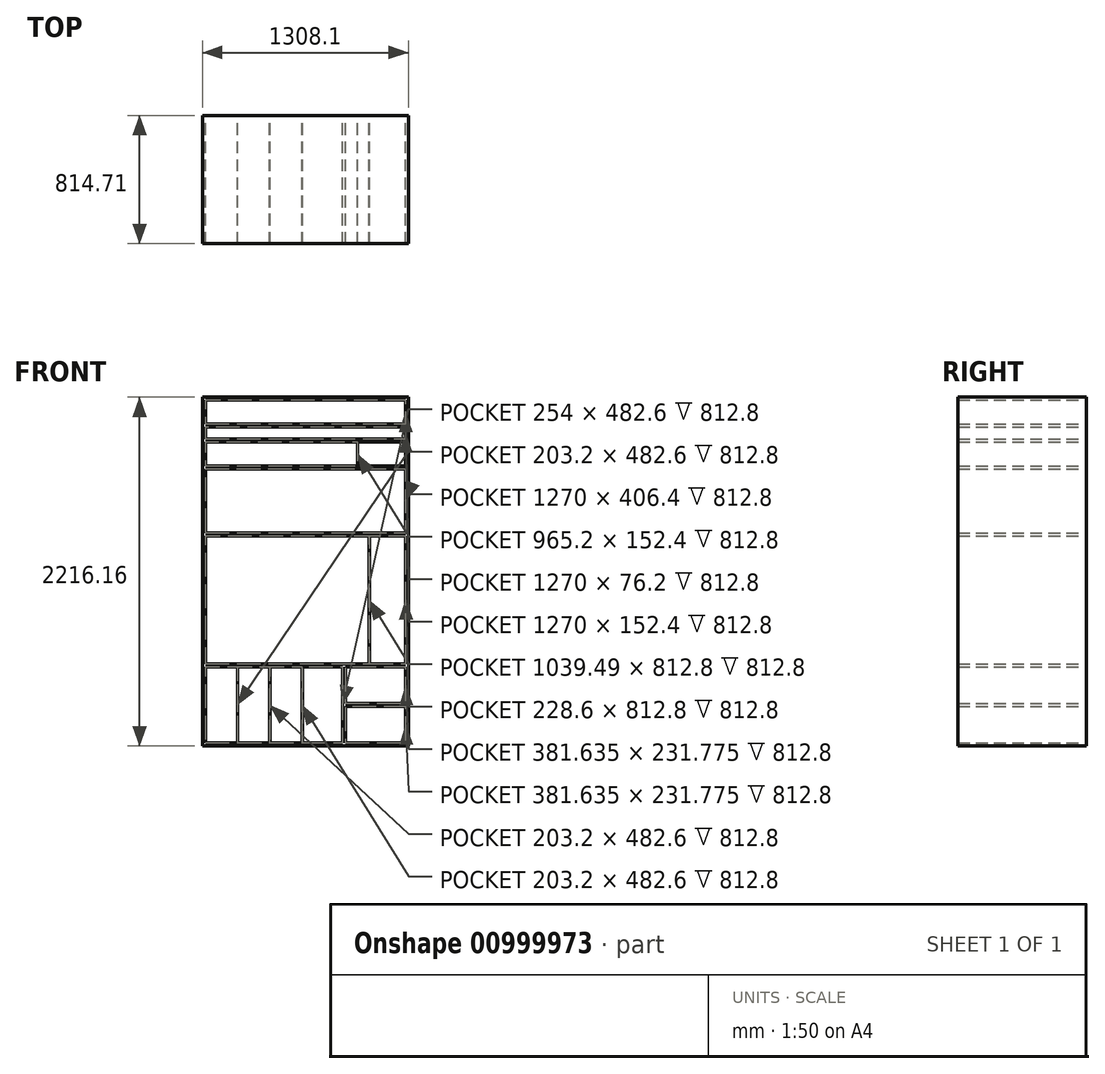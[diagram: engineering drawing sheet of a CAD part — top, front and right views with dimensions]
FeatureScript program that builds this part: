
annotation { "Feature Type Name" : "Feature", "Feature Type Description" : "" }
export const myFeature = defineFeature(function(context is Context, id is Id, definition is map)
    precondition{}
    {
        {
            var Q0;
            Q0=qCreatedBy(makeId("Front.planeOp"),FACE);
            var sketch = newSketch(context, id + "F0", { "sketchPlane" : qUnion([Q0])});
            skLineSegment(sketch, "E0.bottom", {"start": v(-635, 415.93) * mm, "end": v(635, 415.93) * mm});
            skLineSegment(sketch, "E0.top", {"start": v(-635, -415.93) * mm, "end": v(635, -415.92) * mm});
            skLineSegment(sketch, "E0.left", {"start": v(-635, 415.93) * mm, "end": v(-635, -415.93) * mm});
            skLineSegment(sketch, "E0.right", {"start": v(635, 415.93) * mm, "end": v(635, -415.92) * mm});
            skPoint(sketch, "E0.middle", {"position": v(0, 0) * mm});
            skLineSegment(sketch, "E1.top", {"start": v(-635, -898.53) * mm, "end": v(635, -898.52) * mm});
            skLineSegment(sketch, "E1.left", {"start": v(-635, -415.93) * mm, "end": v(-635, -898.53) * mm});
            skLineSegment(sketch, "E1.right", {"start": v(635, -415.92) * mm, "end": v(635, -898.52) * mm});
            skLineSegment(sketch, "E2", {"start": v(-431.8, -415.93) * mm, "end": v(-431.8, -898.52) * mm});
            skLineSegment(sketch, "E3", {"start": v(-226.7, -415.92) * mm, "end": v(-226.7, -898.52) * mm});
            skLineSegment(sketch, "E4", {"start": v(-635, -396.88) * mm, "end": v(635, -396.87) * mm});
            skLineSegment(sketch, "E5.top", {"start": v(-635, -917.58) * mm, "end": v(635, -917.57) * mm});
            skLineSegment(sketch, "E5.left", {"start": v(-635, -898.53) * mm, "end": v(-635, -917.58) * mm});
            skLineSegment(sketch, "E5.right", {"start": v(635, -898.52) * mm, "end": v(635, -917.57) * mm});
            skLineSegment(sketch, "E6", {"start": v(-429.9, -415.93) * mm, "end": v(-429.9, -898.52) * mm});
            skLineSegment(sketch, "E7", {"start": v(-224.8, -415.92) * mm, "end": v(-224.79, -898.52) * mm});
            skLineSegment(sketch, "E8", {"start": v(-21.6, -415.92) * mm, "end": v(-21.59, -898.52) * mm});
            skLineSegment(sketch, "E9", {"start": v(-19.69, -415.92) * mm, "end": v(-19.68, -898.52) * mm});
            skLineSegment(sketch, "E10.top", {"start": v(-635, 434.98) * mm, "end": v(635, 434.98) * mm});
            skLineSegment(sketch, "E10.left", {"start": v(-635, 415.92) * mm, "end": v(-635, 434.98) * mm});
            skLineSegment(sketch, "E10.right", {"start": v(635, 415.93) * mm, "end": v(635, 434.98) * mm});
            skLineSegment(sketch, "E11.top", {"start": v(-635, 841.38) * mm, "end": v(635, 841.38) * mm});
            skLineSegment(sketch, "E11.left", {"start": v(-635, 434.98) * mm, "end": v(-635, 841.38) * mm});
            skLineSegment(sketch, "E11.right", {"start": v(635, 434.98) * mm, "end": v(635, 841.38) * mm});
            skLineSegment(sketch, "E12.top", {"start": v(-635, 860.43) * mm, "end": v(635, 860.43) * mm});
            skLineSegment(sketch, "E12.left", {"start": v(-635, 841.38) * mm, "end": v(-635, 860.43) * mm});
            skLineSegment(sketch, "E12.right", {"start": v(635, 841.38) * mm, "end": v(635, 860.43) * mm});
            skLineSegment(sketch, "E13.bottom", {"start": v(-635, 860.43) * mm, "end": v(0, 860.43) * mm});
            skLineSegment(sketch, "E13.top", {"start": v(-635, 1012.82) * mm, "end": v(0, 1012.82) * mm});
            skLineSegment(sketch, "E13.left", {"start": v(-635, 860.43) * mm, "end": v(-635, 1012.82) * mm});
            skLineSegment(sketch, "E14.bottom", {"start": v(0, 1012.82) * mm, "end": v(635, 1012.82) * mm});
            skLineSegment(sketch, "E14.top", {"start": v(0, 860.43) * mm, "end": v(635, 860.43) * mm});
            skLineSegment(sketch, "E14.right", {"start": v(635, 1012.82) * mm, "end": v(635, 860.43) * mm});
            skLineSegment(sketch, "E15.bottom", {"start": v(-635, 1012.82) * mm, "end": v(635, 1012.82) * mm});
            skLineSegment(sketch, "E15.top", {"start": v(-635, 1031.87) * mm, "end": v(635, 1031.87) * mm});
            skLineSegment(sketch, "E15.left", {"start": v(-635, 1012.82) * mm, "end": v(-635, 1031.87) * mm});
            skLineSegment(sketch, "E15.right", {"start": v(635, 1012.82) * mm, "end": v(635, 1031.87) * mm});
            skLineSegment(sketch, "E16.bottom", {"start": v(-635, 1031.87) * mm, "end": v(635, 1031.88) * mm});
            skLineSegment(sketch, "E16.top", {"start": v(-635, 1279.53) * mm, "end": v(635, 1279.53) * mm});
            skLineSegment(sketch, "E16.left", {"start": v(-635, 1031.87) * mm, "end": v(-635, 1279.53) * mm});
            skLineSegment(sketch, "E16.right", {"start": v(635, 1031.87) * mm, "end": v(635, 1279.53) * mm});
            skLineSegment(sketch, "E17.top", {"start": v(-635, 1298.58) * mm, "end": v(635, 1298.58) * mm});
            skLineSegment(sketch, "E17.left", {"start": v(-635, 1279.53) * mm, "end": v(-635, 1298.58) * mm});
            skLineSegment(sketch, "E17.right", {"start": v(635, 1279.53) * mm, "end": v(635, 1298.58) * mm});
            skLineSegment(sketch, "E18.bottom", {"start": v(635, 1298.58) * mm, "end": v(654.05, 1298.58) * mm});
            skLineSegment(sketch, "E18.top", {"start": v(635, -917.57) * mm, "end": v(654.05, -917.57) * mm});
            skLineSegment(sketch, "E18.left", {"start": v(635, 1298.58) * mm, "end": v(635, -917.57) * mm});
            skLineSegment(sketch, "E18.right", {"start": v(654.05, 1298.58) * mm, "end": v(654.05, -917.58) * mm});
            skLineSegment(sketch, "E19.bottom", {"start": v(-635, -917.58) * mm, "end": v(-654.05, -917.58) * mm});
            skLineSegment(sketch, "E19.top", {"start": v(-635, 1298.58) * mm, "end": v(-654.05, 1298.58) * mm});
            skLineSegment(sketch, "E19.left", {"start": v(-635, -917.58) * mm, "end": v(-635, 1298.58) * mm});
            skLineSegment(sketch, "E19.right", {"start": v(-654.05, -917.58) * mm, "end": v(-654.05, 1298.58) * mm});
            skLineSegment(sketch, "E20", {"start": v(234.31, -415.92) * mm, "end": v(234.32, -898.52) * mm});
            skLineSegment(sketch, "E21", {"start": v(253.36, -415.92) * mm, "end": v(253.37, -898.52) * mm});
            skLineSegment(sketch, "E22", {"start": v(253.37, -666.75) * mm, "end": v(635, -666.75) * mm});
            skLineSegment(sketch, "E23", {"start": v(635, -647.7) * mm, "end": v(253.37, -647.7) * mm});
            skLineSegment(sketch, "E24", {"start": v(406.4, 415.93) * mm, "end": v(406.4, -396.88) * mm});
            skLineSegment(sketch, "E25", {"start": v(404.5, 415.93) * mm, "end": v(404.5, -396.88) * mm});
            skLineSegment(sketch, "E26", {"start": v(330.2, 1012.83) * mm, "end": v(330.2, 860.43) * mm});
            skLineSegment(sketch, "E27", {"start": v(332.1, 1012.83) * mm, "end": v(332.1, 860.43) * mm});
            skLineSegment(sketch, "E28", {"start": v(-635, 1108.08) * mm, "end": v(635, 1108.08) * mm});
            skLineSegment(sketch, "E29", {"start": v(-635, 1127.13) * mm, "end": v(635, 1127.13) * mm});
            skSolve(sketch);
        }
        {
            var Q0;
            {var subQ8=sQuery(id+"F0.wireOp",EDGE,"E19.bottom");Q0=makeQuery(id+"F0.imprint","IMPRINT",FACE,{"disambiguationData":[TD([[makeQuery(id+"F0.imprint","IMPRINT",EDGE,{"derivedFrom":subQ8}),-1.0]])]});}
            var Q1;
            {var subQ0=sQuery(id+"F0.wireOp",EDGE,"E0.bottom");Q1=makeQuery(id+"F0.imprint","IMPRINT",FACE,{"disambiguationData":[TD([[makeQuery(id+"F0.imprint","IMPRINT",EDGE,{"derivedFrom":subQ0}),1.0]])]});}
            var Q2;
            {var subQ4=sQuery(id+"F0.wireOp",EDGE,"E11.top");Q2=makeQuery(id+"F0.imprint","IMPRINT",FACE,{"disambiguationData":[TD([[makeQuery(id+"F0.imprint","IMPRINT",EDGE,{"derivedFrom":subQ4}),1.0]])]});}
            var Q3;
            {var subQ5=sQuery(id+"F0.wireOp",EDGE,"E16.bottom");Q3=makeQuery(id+"F0.imprint","IMPRINT",FACE,{"disambiguationData":[TD([[makeQuery(id+"F0.imprint","IMPRINT",EDGE,{"derivedFrom":subQ5}),-1.0]])]});}
            var Q4;
            {var subQ0=sQuery(id+"F0.wireOp",EDGE,"uuEBU5uM-bvpj-IbMV-0sR6-nunbu0jyylpy.bottom");Q4=makeQuery(id+"F0.imprint","IMPRINT",FACE,{"disambiguationData":[TD([[makeQuery(id+"F0.imprint","IMPRINT",EDGE,{"derivedFrom":subQ0}),1.0]])]});}
            var Q5;
            {var subQ0=sQuery(id+"F0.wireOp",EDGE,"E16.top");Q5=makeQuery(id+"F0.imprint","IMPRINT",FACE,{"disambiguationData":[TD([[makeQuery(id+"F0.imprint","IMPRINT",EDGE,{"derivedFrom":subQ0}),1.0]])]});}
            var Q6;
            {var subQ8=sQuery(id+"F0.wireOp",EDGE,"E18.bottom");Q6=makeQuery(id+"F0.imprint","IMPRINT",FACE,{"disambiguationData":[TD([[makeQuery(id+"F0.imprint","IMPRINT",EDGE,{"derivedFrom":subQ8}),-1.0]])]});}
            var Q7;
            {var subQ7=sQuery(id+"F0.wireOp",EDGE,"E4");Q7=makeQuery(id+"F0.imprint","IMPRINT",FACE,{"disambiguationData":[TD([[makeQuery(id+"F0.imprint","IMPRINT",EDGE,{"derivedFrom":subQ7}),-1.0]])]});}
            var Q8;
            {var subQ10=sQuery(id+"F0.wireOp",EDGE,"E5.top");Q8=makeQuery(id+"F0.imprint","IMPRINT",FACE,{"disambiguationData":[TD([[makeQuery(id+"F0.imprint","IMPRINT",EDGE,{"derivedFrom":subQ10}),1.0]])]});}
            var Q9;
            {var subQ0=sQuery(id+"F0.wireOp",EDGE,"E2");Q9=makeQuery(id+"F0.imprint","IMPRINT",FACE,{"disambiguationData":[TD([[makeQuery(id+"F0.imprint","IMPRINT",EDGE,{"derivedFrom":subQ0}),1.0]])]});}
            var Q10;
            {var subQ0=sQuery(id+"F0.wireOp",EDGE,"E3");Q10=makeQuery(id+"F0.imprint","IMPRINT",FACE,{"disambiguationData":[TD([[makeQuery(id+"F0.imprint","IMPRINT",EDGE,{"derivedFrom":subQ0}),1.0]])]});}
            var Q11;
            {var subQ0=sQuery(id+"F0.wireOp",EDGE,"E8");Q11=makeQuery(id+"F0.imprint","IMPRINT",FACE,{"disambiguationData":[TD([[makeQuery(id+"F0.imprint","IMPRINT",EDGE,{"derivedFrom":subQ0}),1.0]])]});}
            var Q12;
            {var subQ0=sQuery(id+"F0.wireOp",EDGE,"E14.left");Q12=makeQuery(id+"F0.imprint","IMPRINT",FACE,{"disambiguationData":[TD([[makeQuery(id+"F0.imprint","IMPRINT",EDGE,{"derivedFrom":subQ0}),1.0]])]});}
            var Q13;
            {var subQ0=sQuery(id+"F0.wireOp",EDGE,"cd2xjtuK-V6Q1-SAZ6-owor-SNiNtMskj52x");Q13=makeQuery(id+"F0.imprint","IMPRINT",FACE,{"disambiguationData":[TD([[makeQuery(id+"F0.imprint","IMPRINT",EDGE,{"derivedFrom":subQ0}),1.0]])]});}
            var Q14;
            {var subQ0=sQuery(id+"F0.wireOp",EDGE,"E28");Q14=makeQuery(id+"F0.imprint","IMPRINT",FACE,{"disambiguationData":[TD([[makeQuery(id+"F0.imprint","IMPRINT",EDGE,{"derivedFrom":subQ0}),1.0]])]});}
            var Q15;
            {var subQ0=sQuery(id+"F0.wireOp",EDGE,"E26");Q15=makeQuery(id+"F0.imprint","IMPRINT",FACE,{"disambiguationData":[TD([[makeQuery(id+"F0.imprint","IMPRINT",EDGE,{"derivedFrom":subQ0}),1.0]])]});}
            var Q16;
            {var subQ0=sQuery(id+"F0.wireOp",EDGE,"E24");Q16=makeQuery(id+"F0.imprint","IMPRINT",FACE,{"disambiguationData":[TD([[makeQuery(id+"F0.imprint","IMPRINT",EDGE,{"derivedFrom":subQ0}),-1.0]])]});}
            var Q17;
            {var subQ4=sQuery(id+"F0.wireOp",EDGE,"E20");Q17=makeQuery(id+"F0.imprint","IMPRINT",FACE,{"disambiguationData":[TD([[makeQuery(id+"F0.imprint","IMPRINT",EDGE,{"derivedFrom":subQ4}),1.0]])]});}
            var Q18;
            {var subQ0=sQuery(id+"F0.wireOp",EDGE,"E22");Q18=makeQuery(id+"F0.imprint","IMPRINT",FACE,{"disambiguationData":[TD([[makeQuery(id+"F0.imprint","IMPRINT",EDGE,{"derivedFrom":subQ0}),1.0]])]});}
            extrude(context, id + "F1", {"entities" : qUnion([Q0, Q1, Q2, Q3, Q4, Q5, Q6, Q7, Q8, Q9, Q10, Q11, Q12, Q13, Q14, Q15, Q16, Q17, Q18]), "depth" : 812.8 * mm, "offsetDistance" : 25.4 * mm});
        }
        {
            var Q0;
            Q0=makeQuery(id+"F1.opExtrude","CAP_FACE",FACE,{"disambiguationData":[OSD([sQuery(id+"F0.wireOp",EDGE,"E0.top"),sQuery(id+"F0.wireOp",EDGE,"E2"),sQuery(id+"F0.wireOp",EDGE,"E3"),sQuery(id+"F0.wireOp",EDGE,"E4"),sQuery(id+"F0.wireOp",EDGE,"E1.top"),sQuery(id+"F0.wireOp",EDGE,"E5.top"),sQuery(id+"F0.wireOp",EDGE,"E6"),sQuery(id+"F0.wireOp",EDGE,"E7"),sQuery(id+"F0.wireOp",EDGE,"E8"),sQuery(id+"F0.wireOp",EDGE,"E9"),sQuery(id+"F0.wireOp",EDGE,"E0.bottom"),sQuery(id+"F0.wireOp",EDGE,"E10.top"),sQuery(id+"F0.wireOp",EDGE,"E11.top"),sQuery(id+"F0.wireOp",EDGE,"E13.bottom"),sQuery(id+"F0.wireOp",EDGE,"E14.top"),sQuery(id+"F0.wireOp",EDGE,"E15.bottom"),sQuery(id+"F0.wireOp",EDGE,"E16.bottom"),sQuery(id+"F0.wireOp",EDGE,"E16.top"),sQuery(id+"F0.wireOp",EDGE,"E17.top"),sQuery(id+"F0.wireOp",EDGE,"E18.bottom"),sQuery(id+"F0.wireOp",EDGE,"E18.top"),sQuery(id+"F0.wireOp",EDGE,"E18.left"),sQuery(id+"F0.wireOp",EDGE,"E18.right"),sQuery(id+"F0.wireOp",EDGE,"E19.bottom"),sQuery(id+"F0.wireOp",EDGE,"E19.top"),sQuery(id+"F0.wireOp",EDGE,"E19.left"),sQuery(id+"F0.wireOp",EDGE,"E19.right"),sQuery(id+"F0.wireOp",EDGE,"E20"),sQuery(id+"F0.wireOp",EDGE,"E21"),sQuery(id+"F0.wireOp",EDGE,"E22"),sQuery(id+"F0.wireOp",EDGE,"E23"),sQuery(id+"F0.wireOp",EDGE,"E24"),sQuery(id+"F0.wireOp",EDGE,"E25"),sQuery(id+"F0.wireOp",EDGE,"E26"),sQuery(id+"F0.wireOp",EDGE,"E27"),sQuery(id+"F0.wireOp",EDGE,"E28"),sQuery(id+"F0.wireOp",EDGE,"E29")])],"isStart":false});
            var sketch = newSketch(context, id + "F2", { "sketchPlane" : qUnion([Q0])});
            skLineSegment(sketch, "E30.bottom", {"start": v(-654.05, 1298.58) * mm, "end": v(654.05, 1298.58) * mm});
            skLineSegment(sketch, "E30.top", {"start": v(-654.05, -917.57) * mm, "end": v(654.05, -917.57) * mm});
            skLineSegment(sketch, "E30.left", {"start": v(-654.05, 1298.58) * mm, "end": v(-654.05, -917.57) * mm});
            skLineSegment(sketch, "E30.right", {"start": v(654.05, 1298.58) * mm, "end": v(654.05, -917.57) * mm});
            skSolve(sketch);
        }
        {
            var Q0;
            Q0 = qSketchRegion(id + "F2", true);
            extrude(context, id + "F3", {"entities" : qUnion([Q0]), "operationType" : NewBodyOperationType.ADD, "oppositeDirection" : true, "depth" : 814.7 * mm, "offsetDistance" : 25.4 * mm, "hasSecondDirection" : true, "secondDirectionOppositeDirection" : true, "secondDirectionDepth" : 812.8 * mm});
        }
    });
